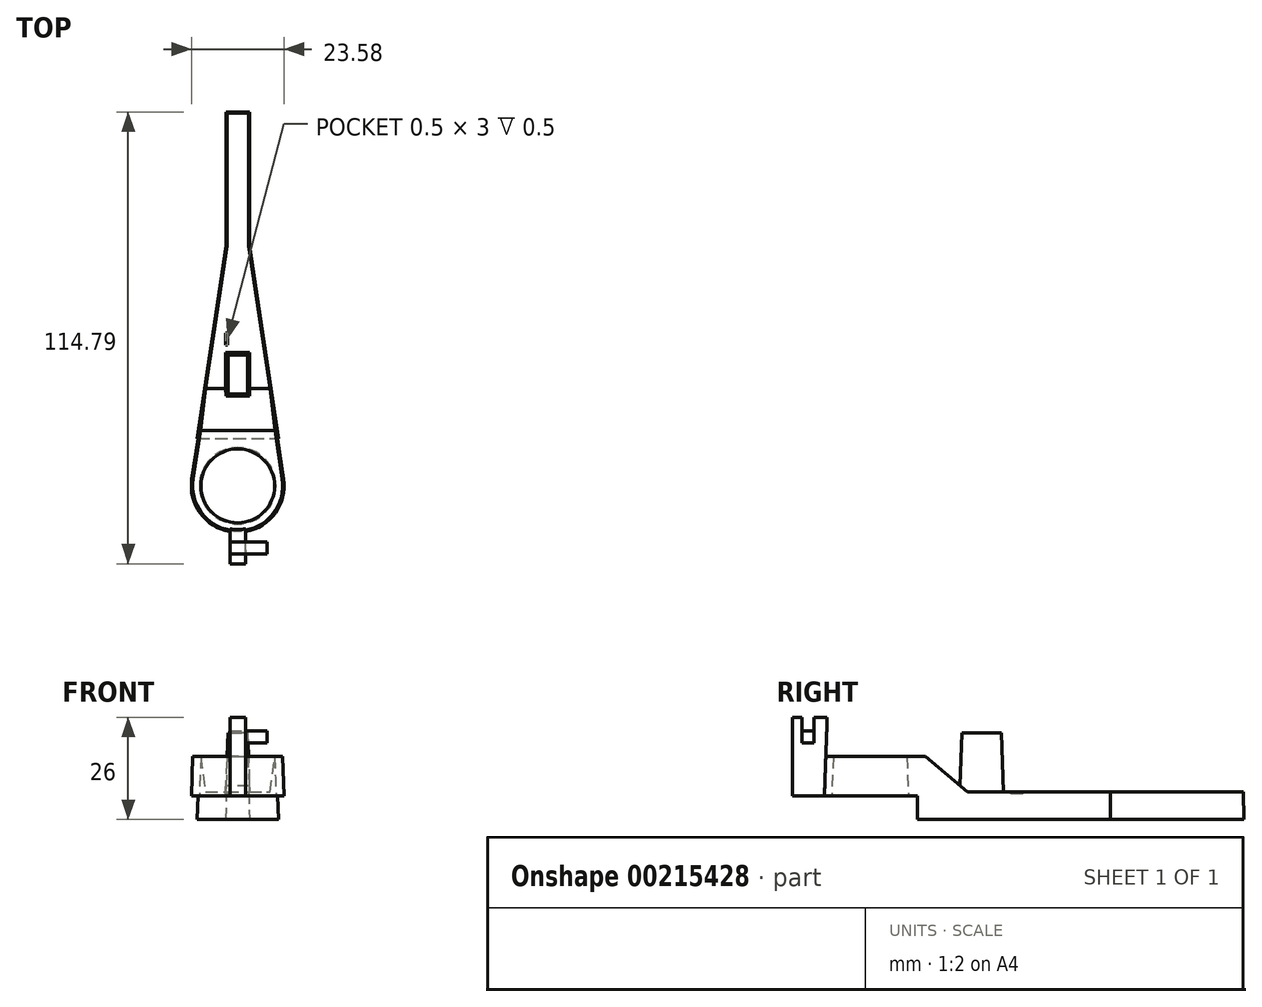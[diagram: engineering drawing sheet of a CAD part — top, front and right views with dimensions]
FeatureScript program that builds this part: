
annotation { "Feature Type Name" : "Feature", "Feature Type Description" : "" }
export const myFeature = defineFeature(function(context is Context, id is Id, definition is map)
    precondition{}
    {
        {
            var Q0;
            Q0=qCreatedBy(makeId("Top.planeOp"),FACE);
            var sketch = newSketch(context, id + "F0", { "sketchPlane" : qUnion([Q0])});
            skCircle(sketch, "E0", {"center": v(0, 0) * mm, "radius": 12 * mm});
            skLineSegment(sketch, "E1", {"start": v(-3, 95) * mm, "end": v(3, 95) * mm});
            skLineSegment(sketch, "E2", {"start": v(0, -12) * mm, "end": v(0, 95) * mm, "construction": true});
            skPoint(sketch, "E3", {"position": v(0, 95) * mm});
            skLineSegment(sketch, "E4", {"start": v(-3, 95) * mm, "end": v(-3, 61) * mm});
            skLineSegment(sketch, "E5", {"start": v(3, 95) * mm, "end": v(3, 61) * mm});
            skLineSegment(sketch, "E6", {"start": v(-3, 61) * mm, "end": v(-11.87, 1.78) * mm});
            skLineSegment(sketch, "E7", {"start": v(3, 61) * mm, "end": v(11.87, 1.78) * mm});
            skSolve(sketch);
        }
        {
            var Q0;
            Q0=qSketchRegion(id+"F0",true);
            extrude(context, id + "F1", {"entities" : qUnion([Q0]), "depth" : 16 * mm, "hasDraft" : true, "draftAngle" : 2 * degree, "draftPullDirection" : true});
        }
        {
            var Q0;
            Q0=qCreatedBy(makeId("Right.planeOp"),FACE);
            cPlane(context, id + "F2", {"entities" : qUnion([Q0]), "cplaneType" : CPlaneType.OFFSET, "offset" : 12 * mm, "width" : 150 * mm, "height" : 150 * mm});
        }
        {
            var Q0;
            Q0=qCreatedBy(id+"F2.planeOp",FACE);
            var sketch = newSketch(context, id + "F3", { "sketchPlane" : qUnion([Q0])});
            skLineSegment(sketch, "E8", {"start": v(94.76, 7) * mm, "end": v(24.76, 7) * mm});
            skLineSegment(sketch, "E9", {"start": v(24.76, 7) * mm, "end": v(14.03, 16) * mm});
            skLineSegment(sketch, "E10", {"start": v(12, 0) * mm, "end": v(12, 6) * mm});
            skLineSegment(sketch, "E11", {"start": v(12, 6) * mm, "end": v(-11.8, 6) * mm});
            skLineSegment(sketch, "E12", {"start": v(12, 0) * mm, "end": v(-12, 0) * mm});
            skLineSegment(sketch, "E13", {"start": v(-12, 0) * mm, "end": v(-11.8, 6) * mm});
            skLineSegment(sketch, "E14", {"start": v(14.03, 16) * mm, "end": v(94.44, 16) * mm});
            skLineSegment(sketch, "E15", {"start": v(94.44, 16) * mm, "end": v(94.76, 7) * mm});
            skSolve(sketch);
        }
        {
            var Q0;
            Q0=qSketchRegion(id+"F3",true);
            extrude(context, id + "F4", {"entities" : qUnion([Q0]), "operationType" : NewBodyOperationType.REMOVE, "endBound" : BoundingType.THROUGH_ALL, "oppositeDirection" : true, "depth" : 25 * mm});
        }
        {
            var Q0;
            Q0=makeQuery(id+"F4.boolean.opBoolean","COPY",FACE,{"derivedFrom":makeQuery(id+"F4.opExtrude","SWEPT_FACE",FACE,{"disambiguationData":[OSD([sQuery(id+"F3.wireOp",EDGE,"E8")])]})});
            cPlane(context, id + "F5", {"entities" : qUnion([Q0]), "cplaneType" : CPlaneType.OFFSET, "offset" : 15 * mm, "width" : 150 * mm, "height" : 150 * mm});
        }
        {
            var Q0;
            Q0=qCreatedBy(id+"F5.planeOp",FACE);
            var sketch = newSketch(context, id + "F6", { "sketchPlane" : qUnion([Q0])});
            skLineSegment(sketch, "E16.bottom", {"start": v(-2.5, 23.3) * mm, "end": v(2.5, 23.3) * mm});
            skLineSegment(sketch, "E16.top", {"start": v(-2.5, 33.3) * mm, "end": v(2.5, 33.3) * mm});
            skLineSegment(sketch, "E16.left", {"start": v(-2.5, 23.3) * mm, "end": v(-2.5, 33.3) * mm});
            skLineSegment(sketch, "E16.right", {"start": v(2.5, 23.3) * mm, "end": v(2.5, 33.3) * mm});
            skPoint(sketch, "E16.middle", {"position": v(0, 28.3) * mm});
            skSolve(sketch);
        }
        {
            var Q0;
            Q0=qSketchRegion(id+"F6",true);
            extrude(context, id + "F7", {"entities" : qUnion([Q0]), "operationType" : NewBodyOperationType.ADD, "endBound" : BoundingType.UP_TO_NEXT, "oppositeDirection" : true, "depth" : 25 * mm, "hasDraft" : true, "draftAngle" : 2 * degree});
        }
        {
            var Q0;
            Q0=makeQuery(id+"F4.boolean.opBoolean","COPY",FACE,{"derivedFrom":makeQuery(id+"F4.opExtrude","SWEPT_FACE",FACE,{"disambiguationData":[OSD([sQuery(id+"F3.wireOp",EDGE,"E11")])]})});
            var sketch = newSketch(context, id + "F8", { "sketchPlane" : qUnion([Q0])});
            skCircle(sketch, "E17", {"center": v(0, 0) * mm, "radius": 9.72 * mm});
            skSolve(sketch);
        }
        {
            var Q0;
            Q0=qSketchRegion(id+"F8",true);
            extrude(context, id + "F9", {"entities" : qUnion([Q0]), "operationType" : NewBodyOperationType.REMOVE, "endBound" : BoundingType.THROUGH_ALL, "oppositeDirection" : true, "depth" : 25 * mm, "hasDraft" : true, "draftAngle" : 2 * degree, "draftPullDirection" : true});
        }
        {
            var Q0;
            Q0=makeQuery(id+"F4.boolean.opBoolean","COPY",FACE,{"derivedFrom":makeQuery(id+"F4.opExtrude","SWEPT_FACE",FACE,{"disambiguationData":[OSD([sQuery(id+"F3.wireOp",EDGE,"E11")])]})});
            var sketch = newSketch(context, id + "F10", { "sketchPlane" : qUnion([Q0])});
            skLineSegment(sketch, "E18", {"start": v(0, 11.8) * mm, "end": v(0, 19.8) * mm, "construction": true});
            skPoint(sketch, "E18.endSnap0", {"position": v(0, 11.8) * mm});
            skLineSegment(sketch, "E19", {"start": v(0, 19.8) * mm, "end": v(-2, 19.8) * mm});
            skLineSegment(sketch, "E20", {"start": v(-2, 19.8) * mm, "end": v(-2, 11.62) * mm});
            skLineSegment(sketch, "E21", {"start": v(0, 19.8) * mm, "end": v(2, 19.8) * mm});
            skLineSegment(sketch, "E22", {"start": v(2, 19.8) * mm, "end": v(2, 11.62) * mm});
            skArc(sketch, "E23", {"start": v(2, 11.62) * mm, "mid": v(0, 11.8) * mm, "end": v(-2, 11.62) * mm});
            skSolve(sketch);
        }
        {
            var Q0;
            Q0=qCreatedBy(makeId("Front.planeOp"),FACE);
            var Q1;
            Q1=sQuery(id+"F10.wireOp",VERTEX,"E21.start");
            cPlane(context, id + "F11", {"entities" : qUnion([Q0, Q1]), "cplaneType" : CPlaneType.PLANE_POINT, "offset" : 25 * mm, "width" : 150 * mm, "height" : 150 * mm});
        }
        {
            var Q0;
            Q0=qCreatedBy(id+"F11.planeOp",FACE);
            var sketch = newSketch(context, id + "F12", { "sketchPlane" : qUnion([Q0])});
            skLineSegment(sketch, "E24.bottom", {"start": v(-2, 6) * mm, "end": v(2, 6) * mm});
            skLineSegment(sketch, "E24.top", {"start": v(-2, 26) * mm, "end": v(2, 26) * mm});
            skLineSegment(sketch, "E24.left", {"start": v(-2, 6) * mm, "end": v(-2, 26) * mm});
            skLineSegment(sketch, "E24.right", {"start": v(2, 6) * mm, "end": v(2, 26) * mm});
            skSolve(sketch);
        }
        {
            var Q0;
            Q0=qSketchRegion(id+"F12",true);
            var Q1;
            Q1=makeQuery(id+"F1.opExtrude","SWEPT_FACE",FACE,{"disambiguationData":[OSD([sQuery(id+"F0.wireOp",EDGE,"E0")])]});
            extrude(context, id + "F13", {"entities" : qUnion([Q0]), "operationType" : NewBodyOperationType.ADD, "endBound" : BoundingType.UP_TO_SURFACE, "oppositeDirection" : true, "endBoundEntityFace" : qUnion([Q1]), "depth" : 8 * mm});
        }
        {
            var Q0;
            Q0=makeQuery(id+"F13.opExtrude","SWEPT_FACE",FACE,{"disambiguationData":[OSD([sQuery(id+"F12.wireOp",EDGE,"E24.right")])]});
            var sketch = newSketch(context, id + "F14", { "sketchPlane" : qUnion([Q0])});
            skLineSegment(sketch, "E25.bottom", {"start": v(-17.3, 22.5) * mm, "end": v(-14.3, 22.5) * mm});
            skLineSegment(sketch, "E25.top", {"start": v(-17.3, 19.5) * mm, "end": v(-14.3, 19.5) * mm});
            skLineSegment(sketch, "E25.left", {"start": v(-17.3, 22.5) * mm, "end": v(-17.3, 19.5) * mm});
            skLineSegment(sketch, "E25.right", {"start": v(-14.3, 22.5) * mm, "end": v(-14.3, 19.5) * mm});
            skSolve(sketch);
        }
        {
            var Q0;
            Q0=qSketchRegion(id+"F14",true);
            extrude(context, id + "F15", {"entities" : qUnion([Q0]), "operationType" : NewBodyOperationType.ADD, "depth" : 5.5 * mm});
        }
        {
            var Q0;
            Q0=makeQuery(id+"F13.opExtrude","SWEPT_FACE",FACE,{"disambiguationData":[OSD([sQuery(id+"F12.wireOp",EDGE,"E24.right")])]});
            var sketch = newSketch(context, id + "F16", { "sketchPlane" : qUnion([Q0])});
            skLineSegment(sketch, "E26.bottom", {"start": v(-17.3, 22.5) * mm, "end": v(-14.3, 22.5) * mm});
            skLineSegment(sketch, "E26.top", {"start": v(-17.3, 26) * mm, "end": v(-14.3, 26) * mm});
            skLineSegment(sketch, "E26.left", {"start": v(-17.3, 22.5) * mm, "end": v(-17.3, 26) * mm});
            skLineSegment(sketch, "E26.right", {"start": v(-14.3, 22.5) * mm, "end": v(-14.3, 26) * mm});
            skSolve(sketch);
        }
        {
            var Q0;
            Q0=qSketchRegion(id+"F16",true);
            extrude(context, id + "F17", {"entities" : qUnion([Q0]), "operationType" : NewBodyOperationType.REMOVE, "endBound" : BoundingType.THROUGH_ALL, "oppositeDirection" : true, "depth" : 25 * mm});
        }
        {
            var Q0;
            Q0=makeQuery(id+"F4.boolean.opBoolean","COPY",FACE,{"derivedFrom":makeQuery(id+"F4.opExtrude","SWEPT_FACE",FACE,{"disambiguationData":[OSD([sQuery(id+"F3.wireOp",EDGE,"E8")])]})});
            var sketch = newSketch(context, id + "F18", { "sketchPlane" : qUnion([Q0])});
            skLineSegment(sketch, "E27.bottom", {"start": v(-3.02, 38.82) * mm, "end": v(-2.52, 38.82) * mm});
            skLineSegment(sketch, "E27.top", {"start": v(-3.02, 35.82) * mm, "end": v(-2.52, 35.82) * mm});
            skLineSegment(sketch, "E27.left", {"start": v(-3.02, 38.82) * mm, "end": v(-3.02, 35.82) * mm});
            skLineSegment(sketch, "E27.right", {"start": v(-2.52, 38.82) * mm, "end": v(-2.52, 35.82) * mm});
            skSolve(sketch);
        }
        {
            var Q0;
            Q0 = qSketchRegion(id + "F18", true);
            extrude(context, id + "F19", {"entities" : qUnion([Q0]), "operationType" : NewBodyOperationType.REMOVE, "oppositeDirection" : true, "depth" : 0.5 * mm});
        }
    });
